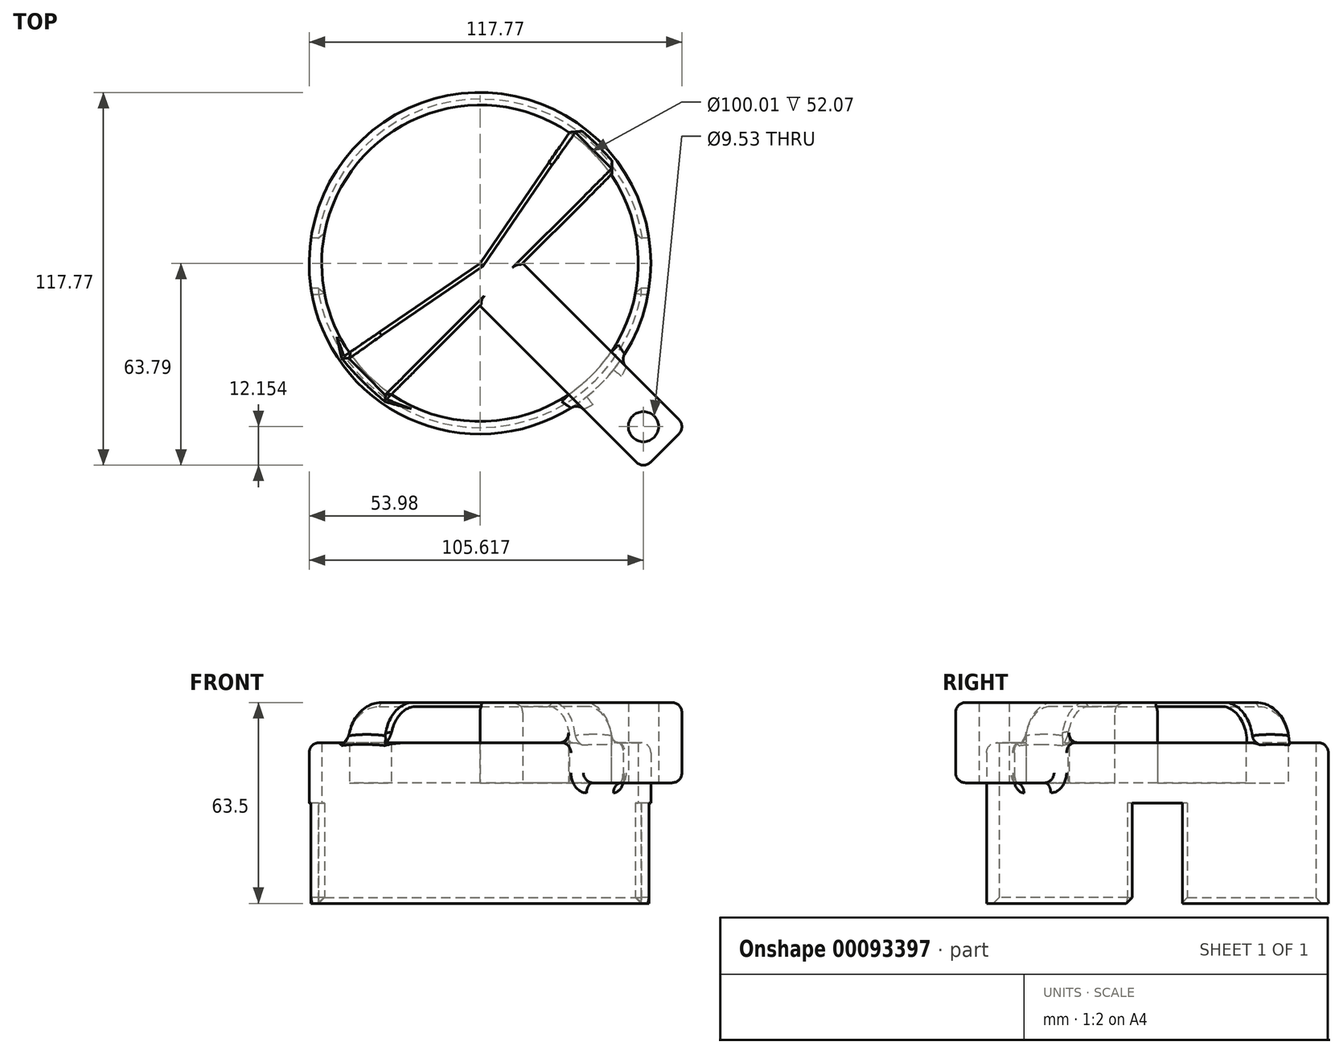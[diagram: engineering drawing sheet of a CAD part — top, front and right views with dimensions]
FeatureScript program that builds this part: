
annotation { "Feature Type Name" : "Feature", "Feature Type Description" : "" }
export const myFeature = defineFeature(function(context is Context, id is Id, definition is map)
    precondition{}
    {
        {
            var Q0;
            Q0=qCreatedBy(makeId("Top.planeOp"),FACE);
            var sketch = newSketch(context, id + "F0", { "sketchPlane" : qUnion([Q0])});
            skCircle(sketch, "E0", {"center": v(0, 0) * mm, "radius": 50 * mm});
            skCircle(sketch, "E1", {"center": v(0, 0) * mm, "radius": 53.98 * mm});
            skLineSegment(sketch, "E2", {"start": v(-113.56, 0) * mm, "end": v(123.98, 0) * mm, "construction": true});
            skSolve(sketch);
        }
        {
            var Q0;
            Q0=qSketchRegion(id+"F0",true);
            extrude(context, id + "F1", {"entities" : qUnion([Q0]), "depth" : 50.8 * mm});
        }
        {
            var Q0;
            Q0=makeQuery(id+"F1.opExtrude","CAP_FACE",FACE,{"disambiguationData":[OSD([sQuery(id+"F0.wireOp",EDGE,"E0"),sQuery(id+"F0.wireOp",EDGE,"E1")])],"isStart":true});
            var sketch = newSketch(context, id + "F2", { "sketchPlane" : qUnion([Q0])});
            skLineSegment(sketch, "E3.bottom", {"start": v(61.76, 7.94) * mm, "end": v(-61.76, 7.94) * mm});
            skLineSegment(sketch, "E3.top", {"start": v(61.76, -7.94) * mm, "end": v(-61.76, -7.94) * mm});
            skLineSegment(sketch, "E3.left", {"start": v(61.76, 7.94) * mm, "end": v(61.76, -7.94) * mm});
            skLineSegment(sketch, "E3.right", {"start": v(-61.76, 7.94) * mm, "end": v(-61.76, -7.94) * mm});
            skPoint(sketch, "E3.middle", {"position": v(0, 0) * mm});
            skSolve(sketch);
        }
        {
            var Q0;
            Q0=qSketchRegion(id+"F2",true);
            extrude(context, id + "F3", {"entities" : qUnion([Q0]), "operationType" : NewBodyOperationType.REMOVE, "oppositeDirection" : true, "depth" : 31.75 * mm});
        }
        {
            var Q0;
            Q0=makeQuery(id+"F1.opExtrude","CAP_FACE",FACE,{"disambiguationData":[OSD([sQuery(id+"F0.wireOp",EDGE,"E0"),sQuery(id+"F0.wireOp",EDGE,"E1")])],"isStart":false});
            var sketch = newSketch(context, id + "F4", { "sketchPlane" : qUnion([Q0])});
            skLineSegment(sketch, "E4", {"start": v(0, 0) * mm, "end": v(80.82, 0) * mm});
            skLineSegment(sketch, "E5", {"start": v(0, 0) * mm, "end": v(59.01, -59.01) * mm});
            skLineSegment(sketch, "E6", {"start": v(0, 0) * mm, "end": v(6.74, 6.74) * mm});
            skLineSegment(sketch, "E7", {"start": v(6.74, 6.74) * mm, "end": v(65.1, -51.64) * mm});
            skLineSegment(sketch, "E8", {"start": v(65.1, -51.64) * mm, "end": v(51.64, -65.1) * mm});
            skLineSegment(sketch, "E9", {"start": v(51.64, -65.1) * mm, "end": v(-6.74, -6.74) * mm});
            skLineSegment(sketch, "E10", {"start": v(-6.74, -6.74) * mm, "end": v(0, 0) * mm});
            skCircle(sketch, "E11", {"center": v(51.64, -51.64) * mm, "radius": 4.76 * mm});
            skSolve(sketch);
        }
        {
            var Q0;
            Q0=qSketchRegion(id+"F4",true);
            extrude(context, id + "F5", {"entities" : qUnion([Q0]), "operationType" : NewBodyOperationType.ADD, "endBound" : BoundingType.SYMMETRIC, "depth" : 25.4 * mm});
        }
        {
            var Q0;
            Q0=makeQuery(id+"F1.opExtrude","CAP_FACE",FACE,{"disambiguationData":[OSD([sQuery(id+"F0.wireOp",EDGE,"E0"),sQuery(id+"F0.wireOp",EDGE,"E1")])],"isStart":false});
            var sketch = newSketch(context, id + "F6", { "sketchPlane" : qUnion([Q0])});
            skLineSegment(sketch, "E12", {"start": v(0, 0) * mm, "end": v(1.72, 1.72) * mm});
            skLineSegment(sketch, "E13", {"start": v(35.92, 35.92) * mm, "end": v(42.66, 29.19) * mm});
            skLineSegment(sketch, "E14", {"start": v(42.66, 29.19) * mm, "end": v(-29.19, -42.66) * mm});
            skLineSegment(sketch, "E15", {"start": v(-29.19, -42.66) * mm, "end": v(-35.92, -35.92) * mm});
            skLineSegment(sketch, "E16", {"start": v(35.92, 35.92) * mm, "end": v(29.19, 42.66) * mm});
            skLineSegment(sketch, "E17", {"start": v(-35.92, -35.92) * mm, "end": v(-42.66, -29.19) * mm});
            skLineSegment(sketch, "E18", {"start": v(0, 0) * mm, "end": v(29.19, 42.66) * mm});
            skLineSegment(sketch, "E19", {"start": v(0, 0) * mm, "end": v(-42.66, -29.19) * mm});
            skSolve(sketch);
        }
        {
            var Q0;
            Q0=qSketchRegion(id+"F6",true);
            extrude(context, id + "F7", {"entities" : qUnion([Q0]), "operationType" : NewBodyOperationType.ADD, "endBound" : BoundingType.SYMMETRIC, "depth" : 25.4 * mm});
        }
        {
            var Q0;
            Q0=makeQuery(id+"F7.opExtrude","CAP_EDGE",EDGE,{"disambiguationData":[OSD([sQuery(id+"F6.wireOp",EDGE,"E13"),sQuery(id+"F6.wireOp",EDGE,"E16")])],"isStart":false});
            var Q1;
            Q1=makeQuery(id+"F7.opExtrude","CAP_EDGE",EDGE,{"disambiguationData":[OSD([sQuery(id+"F6.wireOp",EDGE,"E15"),sQuery(id+"F6.wireOp",EDGE,"E17")])],"isStart":false});
            fillet(context, id + "F8", {"entities" : qUnion([Q0, Q1]), "radius" : 12.7 * mm, "tangentPropagation" : true, "allowEdgeOverflow" : false});
        }
        {
            var Q0;
            Q0=makeQuery(id+"F1.opExtrude","CAP_EDGE",EDGE,{"disambiguationData":[OSD([sQuery(id+"F0.wireOp",EDGE,"E1")])],"isStart":false});
            fillet(context, id + "F9", {"entities" : qUnion([Q0]), "radius" : 3.17 * mm, "tangentPropagation" : true, "allowEdgeOverflow" : false});
        }
        {
            var Q0;
            {var subQ0=sQuery(id+"F0.wireOp",EDGE,"E0");Q0=makeQuery(id+"F3.boolean.opBoolean","SPLIT",EDGE,{"disambiguationData":[TD([makeQuery(id+"F3.opExtrude","SWEPT_FACE",FACE,{"disambiguationData":[OSD([sQuery(id+"F2.wireOp",EDGE,"E3.bottom")])]})])],"derivedFrom":makeQuery(id+"F1.opExtrude","CAP_EDGE",EDGE,{"disambiguationData":[OSD([subQ0])],"isStart":true})});}
            var Q1;
            {var subQ0=sQuery(id+"F0.wireOp",EDGE,"E0");Q1=makeQuery(id+"F3.boolean.opBoolean","SPLIT",EDGE,{"disambiguationData":[TD([makeQuery(id+"F3.opExtrude","SWEPT_FACE",FACE,{"disambiguationData":[OSD([sQuery(id+"F2.wireOp",EDGE,"E3.top")])]})])],"derivedFrom":makeQuery(id+"F1.opExtrude","CAP_EDGE",EDGE,{"disambiguationData":[OSD([subQ0])],"isStart":true})});}
            var Q2;
            Q2=makeQuery(id+"F3.boolean.opBoolean","COPY",EDGE,{"disambiguationData":[OD(1.0)],"derivedFrom":makeQuery(id+"F3.opExtrude","CAP_EDGE",EDGE,{"disambiguationData":[OSD([sQuery(id+"F2.wireOp",EDGE,"E3.bottom")])],"isStart":true})});
            var Q3;
            Q3=makeQuery(id+"F3.boolean.opBoolean","COPY",EDGE,{"disambiguationData":[OD(1.0)],"derivedFrom":makeQuery(id+"F3.opExtrude","CAP_EDGE",EDGE,{"disambiguationData":[OSD([sQuery(id+"F2.wireOp",EDGE,"E3.top")])],"isStart":true})});
            var Q4;
            Q4=makeQuery(id+"F3.boolean.opBoolean","COPY",EDGE,{"disambiguationData":[OD(0.0)],"derivedFrom":makeQuery(id+"F3.opExtrude","CAP_EDGE",EDGE,{"disambiguationData":[OSD([sQuery(id+"F2.wireOp",EDGE,"E3.bottom")])],"isStart":true})});
            var Q5;
            Q5=makeQuery(id+"F3.boolean.opBoolean","COPY",EDGE,{"disambiguationData":[OD(0.0)],"derivedFrom":makeQuery(id+"F3.opExtrude","CAP_EDGE",EDGE,{"disambiguationData":[OSD([sQuery(id+"F2.wireOp",EDGE,"E3.top")])],"isStart":true})});
            var Q6;
            Q6=makeQuery(id+"F3.boolean.opBoolean","INTERSECT",EDGE,{"disambiguationData":[OD(0.0)],"derivedFrom":[makeQuery(id+"F1.opExtrude","SWEPT_FACE",FACE,{"disambiguationData":[OSD([sQuery(id+"F0.wireOp",EDGE,"E0")])]}),makeQuery(id+"F3.opExtrude","SWEPT_FACE",FACE,{"disambiguationData":[OSD([sQuery(id+"F2.wireOp",EDGE,"E3.bottom")])]})]});
            var Q7;
            Q7=makeQuery(id+"F3.boolean.opBoolean","INTERSECT",EDGE,{"disambiguationData":[OD(0.0)],"derivedFrom":[makeQuery(id+"F1.opExtrude","SWEPT_FACE",FACE,{"disambiguationData":[OSD([sQuery(id+"F0.wireOp",EDGE,"E0")])]}),makeQuery(id+"F3.opExtrude","SWEPT_FACE",FACE,{"disambiguationData":[OSD([sQuery(id+"F2.wireOp",EDGE,"E3.top")])]})]});
            var Q8;
            Q8=makeQuery(id+"F3.boolean.opBoolean","INTERSECT",EDGE,{"disambiguationData":[OD(1.0)],"derivedFrom":[makeQuery(id+"F1.opExtrude","SWEPT_FACE",FACE,{"disambiguationData":[OSD([sQuery(id+"F0.wireOp",EDGE,"E0")])]}),makeQuery(id+"F3.opExtrude","SWEPT_FACE",FACE,{"disambiguationData":[OSD([sQuery(id+"F2.wireOp",EDGE,"E3.bottom")])]})]});
            var Q9;
            Q9=makeQuery(id+"F3.boolean.opBoolean","INTERSECT",EDGE,{"disambiguationData":[OD(1.0)],"derivedFrom":[makeQuery(id+"F1.opExtrude","SWEPT_FACE",FACE,{"disambiguationData":[OSD([sQuery(id+"F0.wireOp",EDGE,"E0")])]}),makeQuery(id+"F3.opExtrude","SWEPT_FACE",FACE,{"disambiguationData":[OSD([sQuery(id+"F2.wireOp",EDGE,"E3.top")])]})]});
            chamfer(context, id + "F10", {"entities" : qUnion([Q0, Q1, Q2, Q3, Q4, Q5, Q6, Q7, Q8, Q9]), "width" : 1.9 * mm, "tangentPropagation" : true});
        }
        {
            var Q0;
            Q0=makeQuery(id+"F5.opExtrude","CAP_EDGE",EDGE,{"disambiguationData":[OSD([sQuery(id+"F4.wireOp",EDGE,"E9")])],"isStart":false});
            var Q1;
            Q1=makeQuery(id+"F5.opExtrude","CAP_EDGE",EDGE,{"disambiguationData":[OSD([sQuery(id+"F4.wireOp",EDGE,"E7")])],"isStart":false});
            var Q2;
            Q2=makeQuery(id+"F5.opExtrude","CAP_EDGE",EDGE,{"disambiguationData":[OSD([sQuery(id+"F4.wireOp",EDGE,"E8")])],"isStart":false});
            var Q3;
            Q3=makeQuery(id+"F5.opExtrude","SWEPT_EDGE",EDGE,{"disambiguationData":[OSD([sQuery(id+"F4.wireOp",EDGE,"E8"),sQuery(id+"F4.wireOp",EDGE,"E9")])]});
            var Q4;
            Q4=makeQuery(id+"F5.opExtrude","SWEPT_EDGE",EDGE,{"disambiguationData":[OSD([sQuery(id+"F4.wireOp",EDGE,"E7"),sQuery(id+"F4.wireOp",EDGE,"E8")])]});
            var Q5;
            Q5=makeQuery(id+"F5.boolean.opBoolean","INTERSECT",EDGE,{"derivedFrom":[makeQuery(id+"F1.opExtrude","SWEPT_FACE",FACE,{"disambiguationData":[OSD([sQuery(id+"F0.wireOp",EDGE,"E1")])]}),makeQuery(id+"F5.opExtrude","CAP_FACE",FACE,{"disambiguationData":[OSD([sQuery(id+"F4.wireOp",EDGE,"E6"),sQuery(id+"F4.wireOp",EDGE,"E7"),sQuery(id+"F4.wireOp",EDGE,"E8"),sQuery(id+"F4.wireOp",EDGE,"E9"),sQuery(id+"F4.wireOp",EDGE,"E10"),sQuery(id+"F4.wireOp",EDGE,"E11")])],"isStart":true})]});
            var Q6;
            Q6=makeQuery(id+"F5.boolean.opBoolean","INTERSECT",EDGE,{"derivedFrom":[makeQuery(id+"F1.opExtrude","SWEPT_FACE",FACE,{"disambiguationData":[OSD([sQuery(id+"F0.wireOp",EDGE,"E1")])]}),makeQuery(id+"F5.opExtrude","SWEPT_FACE",FACE,{"disambiguationData":[OSD([sQuery(id+"F4.wireOp",EDGE,"E9")])]})]});
            var Q7;
            Q7=makeQuery(id+"F5.boolean.opBoolean","INTERSECT",EDGE,{"derivedFrom":[makeQuery(id+"F1.opExtrude","SWEPT_FACE",FACE,{"disambiguationData":[OSD([sQuery(id+"F0.wireOp",EDGE,"E1")])]}),makeQuery(id+"F5.opExtrude","SWEPT_FACE",FACE,{"disambiguationData":[OSD([sQuery(id+"F4.wireOp",EDGE,"E7")])]})]});
            var Q8;
            {var subQ1=sQuery(id+"F4.wireOp",EDGE,"E7");Q8=makeQuery(id+"F5.boolean.opBoolean","SPLIT",EDGE,{"disambiguationData":[TD([makeQuery(id+"F1.opExtrude","SWEPT_FACE",FACE,{"disambiguationData":[OSD([sQuery(id+"F0.wireOp",EDGE,"E1")])]})])],"derivedFrom":makeQuery(id+"F5.opExtrude","CAP_EDGE",EDGE,{"disambiguationData":[OSD([subQ1])],"isStart":true})});}
            var Q9;
            Q9=makeQuery(id+"F5.opExtrude","CAP_EDGE",EDGE,{"disambiguationData":[OSD([sQuery(id+"F4.wireOp",EDGE,"E8")])],"isStart":true});
            var Q10;
            {var subQ0=sQuery(id+"F4.wireOp",EDGE,"E9");Q10=makeQuery(id+"F5.boolean.opBoolean","SPLIT",EDGE,{"disambiguationData":[TD([makeQuery(id+"F1.opExtrude","SWEPT_FACE",FACE,{"disambiguationData":[OSD([sQuery(id+"F0.wireOp",EDGE,"E1")])]})])],"derivedFrom":makeQuery(id+"F5.opExtrude","CAP_EDGE",EDGE,{"disambiguationData":[OSD([subQ0])],"isStart":true})});}
            fillet(context, id + "F11", {"entities" : qUnion([Q0, Q1, Q2, Q3, Q4, Q5, Q6, Q7, Q8, Q9, Q10]), "radius" : 3.17 * mm, "tangentPropagation" : true, "allowEdgeOverflow" : false});
        }
        {
            var Q0;
            {var subQ4=sQuery(id+"F4.wireOp",EDGE,"E7");var subQ7=sQuery(id+"F6.wireOp",EDGE,"E16");var subQ8=sQuery(id+"F6.wireOp",EDGE,"E13");var subQ13=sQuery(id+"F6.wireOp",EDGE,"E14");Q0=makeQuery(id+"F8.opFillet","BLEND_EDGE",EDGE,{"blendedFrom":[makeQuery(id+"F7.opExtrude","CAP_EDGE",EDGE,{"disambiguationData":[OSD([subQ8,subQ7])],"isStart":false}),makeQuery(id+"F7.boolean.opBoolean","SPLIT",FACE,{"disambiguationData":[TD([makeQuery(id+"F5.opExtrude","SWEPT_FACE",FACE,{"disambiguationData":[OSD([subQ4])]})])],"derivedFrom":makeQuery(id+"F7.opExtrude","SWEPT_FACE",FACE,{"disambiguationData":[OSD([subQ13])]})})],"blendedInto":[makeQuery(id+"F7.boolean.opBoolean","SPLIT",FACE,{"disambiguationData":[TD([makeQuery(id+"F5.opExtrude","SWEPT_FACE",FACE,{"disambiguationData":[OSD([subQ4])]})])],"derivedFrom":makeQuery(id+"F7.opExtrude","SWEPT_FACE",FACE,{"disambiguationData":[OSD([subQ13])]})})]});}
            var Q1;
            {var subQ0=sQuery(id+"F6.wireOp",EDGE,"E14");var subQ3=sQuery(id+"F4.wireOp",EDGE,"E9");Q1=makeQuery(id+"F7.boolean.opBoolean","SPLIT",EDGE,{"disambiguationData":[TD([makeQuery(id+"F5.opExtrude","SWEPT_FACE",FACE,{"disambiguationData":[OSD([subQ3])]})])],"derivedFrom":makeQuery(id+"F7.opExtrude","CAP_EDGE",EDGE,{"disambiguationData":[OSD([subQ0])],"isStart":false})});}
            var Q2;
            Q2=makeQuery(id+"F7.opExtrude","CAP_EDGE",EDGE,{"disambiguationData":[OSD([sQuery(id+"F6.wireOp",EDGE,"E19")])],"isStart":false});
            var Q3;
            Q3=makeQuery(id+"F7.opExtrude","CAP_EDGE",EDGE,{"disambiguationData":[OSD([sQuery(id+"F6.wireOp",EDGE,"E18")])],"isStart":false});
            chamfer(context, id + "F12", {"entities" : qUnion([Q0, Q1, Q2, Q3]), "width" : 1.27 * mm, "tangentPropagation" : true});
        }
        {
            var Q0;
            Q0=makeQuery(id+"F9.opFillet","BLEND_EDGE",EDGE,{"disambiguationData":[OD(0.0)],"blendedFrom":[makeQuery(id+"F1.opExtrude","CAP_EDGE",EDGE,{"disambiguationData":[OSD([sQuery(id+"F0.wireOp",EDGE,"E1")])],"isStart":false}),makeQuery(id+"F8.opFillet","BLEND_FACE",FACE,{"disambiguationData":[OSD([sQuery(id+"F6.wireOp",EDGE,"E13"),sQuery(id+"F6.wireOp",EDGE,"E16")])]})],"blendedInto":[makeQuery(id+"F8.opFillet","BLEND_FACE",FACE,{"disambiguationData":[OSD([sQuery(id+"F6.wireOp",EDGE,"E13"),sQuery(id+"F6.wireOp",EDGE,"E16")])]})]});
            var Q1;
            Q1=makeQuery(id+"F9.opFillet","BLEND_EDGE",EDGE,{"disambiguationData":[OD(1.0)],"blendedFrom":[makeQuery(id+"F1.opExtrude","CAP_EDGE",EDGE,{"disambiguationData":[OSD([sQuery(id+"F0.wireOp",EDGE,"E1")])],"isStart":false}),makeQuery(id+"F8.opFillet","BLEND_FACE",FACE,{"disambiguationData":[OSD([sQuery(id+"F6.wireOp",EDGE,"E15"),sQuery(id+"F6.wireOp",EDGE,"E17")])]})],"blendedInto":[makeQuery(id+"F8.opFillet","BLEND_FACE",FACE,{"disambiguationData":[OSD([sQuery(id+"F6.wireOp",EDGE,"E15"),sQuery(id+"F6.wireOp",EDGE,"E17")])]})]});
            var Q2;
            Q2=makeQuery(id+"F12.opChamfer","BLEND_EDGE",EDGE,{"blendedFrom":[makeQuery(id+"F8.opFillet","BLEND_EDGE",EDGE,{"blendedFrom":[makeQuery(id+"F7.opExtrude","CAP_EDGE",EDGE,{"disambiguationData":[OSD([sQuery(id+"F6.wireOp",EDGE,"E15"),sQuery(id+"F6.wireOp",EDGE,"E17")])],"isStart":false}),makeQuery(id+"F7.opExtrude","SWEPT_FACE",FACE,{"disambiguationData":[OSD([sQuery(id+"F6.wireOp",EDGE,"E19")])]})],"blendedInto":[makeQuery(id+"F7.opExtrude","SWEPT_FACE",FACE,{"disambiguationData":[OSD([sQuery(id+"F6.wireOp",EDGE,"E19")])]})]}),makeQuery(id+"F9.opFillet","BLEND_FACE",FACE,{"disambiguationData":[OSD([sQuery(id+"F0.wireOp",EDGE,"E1")])]})],"blendedInto":[makeQuery(id+"F9.opFillet","BLEND_FACE",FACE,{"disambiguationData":[OSD([sQuery(id+"F0.wireOp",EDGE,"E1")])]})]});
            var Q3;
            {var subQ0=sQuery(id+"F0.wireOp",EDGE,"E1");var subQ3=sQuery(id+"F4.wireOp",EDGE,"E9");var subQ10=sQuery(id+"F6.wireOp",EDGE,"E17");var subQ12=sQuery(id+"F6.wireOp",EDGE,"E15");var subQ13=sQuery(id+"F6.wireOp",EDGE,"E14");Q3=makeQuery(id+"F12.opChamfer","BLEND_EDGE",EDGE,{"blendedFrom":[makeQuery(id+"F8.opFillet","BLEND_EDGE",EDGE,{"blendedFrom":[makeQuery(id+"F7.opExtrude","CAP_EDGE",EDGE,{"disambiguationData":[OSD([subQ12,subQ10])],"isStart":false}),makeQuery(id+"F7.boolean.opBoolean","SPLIT",FACE,{"disambiguationData":[TD([makeQuery(id+"F5.opExtrude","SWEPT_FACE",FACE,{"disambiguationData":[OSD([subQ3])]})])],"derivedFrom":makeQuery(id+"F7.opExtrude","SWEPT_FACE",FACE,{"disambiguationData":[OSD([subQ13])]})})],"blendedInto":[makeQuery(id+"F7.boolean.opBoolean","SPLIT",FACE,{"disambiguationData":[TD([makeQuery(id+"F5.opExtrude","SWEPT_FACE",FACE,{"disambiguationData":[OSD([subQ3])]})])],"derivedFrom":makeQuery(id+"F7.opExtrude","SWEPT_FACE",FACE,{"disambiguationData":[OSD([subQ13])]})})]}),makeQuery(id+"F9.opFillet","BLEND_FACE",FACE,{"disambiguationData":[OSD([subQ0])]})],"blendedInto":[makeQuery(id+"F9.opFillet","BLEND_FACE",FACE,{"disambiguationData":[OSD([subQ0])]})]});}
            var Q4;
            Q4=makeQuery(id+"F12.opChamfer","BLEND_EDGE",EDGE,{"blendedFrom":[makeQuery(id+"F8.opFillet","BLEND_EDGE",EDGE,{"blendedFrom":[makeQuery(id+"F7.opExtrude","CAP_EDGE",EDGE,{"disambiguationData":[OSD([sQuery(id+"F6.wireOp",EDGE,"E13"),sQuery(id+"F6.wireOp",EDGE,"E16")])],"isStart":false}),makeQuery(id+"F7.opExtrude","SWEPT_FACE",FACE,{"disambiguationData":[OSD([sQuery(id+"F6.wireOp",EDGE,"E18")])]})],"blendedInto":[makeQuery(id+"F7.opExtrude","SWEPT_FACE",FACE,{"disambiguationData":[OSD([sQuery(id+"F6.wireOp",EDGE,"E18")])]})]}),makeQuery(id+"F9.opFillet","SPLIT",FACE,{"disambiguationData":[OD(2.0)],"derivedFrom":makeQuery(id+"F1.opExtrude","CAP_FACE",FACE,{"disambiguationData":[OSD([sQuery(id+"F0.wireOp",EDGE,"E0"),sQuery(id+"F0.wireOp",EDGE,"E1")])],"isStart":false})})],"blendedInto":[makeQuery(id+"F9.opFillet","SPLIT",FACE,{"disambiguationData":[OD(2.0)],"derivedFrom":makeQuery(id+"F1.opExtrude","CAP_FACE",FACE,{"disambiguationData":[OSD([sQuery(id+"F0.wireOp",EDGE,"E0"),sQuery(id+"F0.wireOp",EDGE,"E1")])],"isStart":false})})]});
            var Q5;
            {var subQ0=sQuery(id+"F0.wireOp",EDGE,"E0");var subQ1=makeQuery(id+"F1.opExtrude","CAP_FACE",FACE,{"disambiguationData":[OSD([subQ0,sQuery(id+"F0.wireOp",EDGE,"E1")])],"isStart":false});var subQ6=sQuery(id+"F4.wireOp",EDGE,"E7");var subQ8=sQuery(id+"F6.wireOp",EDGE,"E16");var subQ9=sQuery(id+"F6.wireOp",EDGE,"E13");var subQ14=sQuery(id+"F6.wireOp",EDGE,"E14");Q5=makeQuery(id+"F12.opChamfer","BLEND_EDGE",EDGE,{"blendedFrom":[makeQuery(id+"F8.opFillet","BLEND_EDGE",EDGE,{"blendedFrom":[makeQuery(id+"F7.opExtrude","CAP_EDGE",EDGE,{"disambiguationData":[OSD([subQ9,subQ8])],"isStart":false}),makeQuery(id+"F7.boolean.opBoolean","SPLIT",FACE,{"disambiguationData":[TD([makeQuery(id+"F5.opExtrude","SWEPT_FACE",FACE,{"disambiguationData":[OSD([subQ6])]})])],"derivedFrom":makeQuery(id+"F7.opExtrude","SWEPT_FACE",FACE,{"disambiguationData":[OSD([subQ14])]})})],"blendedInto":[makeQuery(id+"F7.boolean.opBoolean","SPLIT",FACE,{"disambiguationData":[TD([makeQuery(id+"F5.opExtrude","SWEPT_FACE",FACE,{"disambiguationData":[OSD([subQ6])]})])],"derivedFrom":makeQuery(id+"F7.opExtrude","SWEPT_FACE",FACE,{"disambiguationData":[OSD([subQ14])]})})]}),makeQuery(id+"F9.opFillet","SPLIT",FACE,{"disambiguationData":[OD(0.0)],"derivedFrom":subQ1})],"blendedInto":[makeQuery(id+"F9.opFillet","SPLIT",FACE,{"disambiguationData":[OD(0.0)],"derivedFrom":subQ1})]});}
            fillet(context, id + "F13", {"entities" : qUnion([Q0, Q1, Q2, Q3, Q4, Q5]), "radius" : 5.08 * mm, "tangentPropagation" : true, "allowEdgeOverflow" : false});
        }
    });
